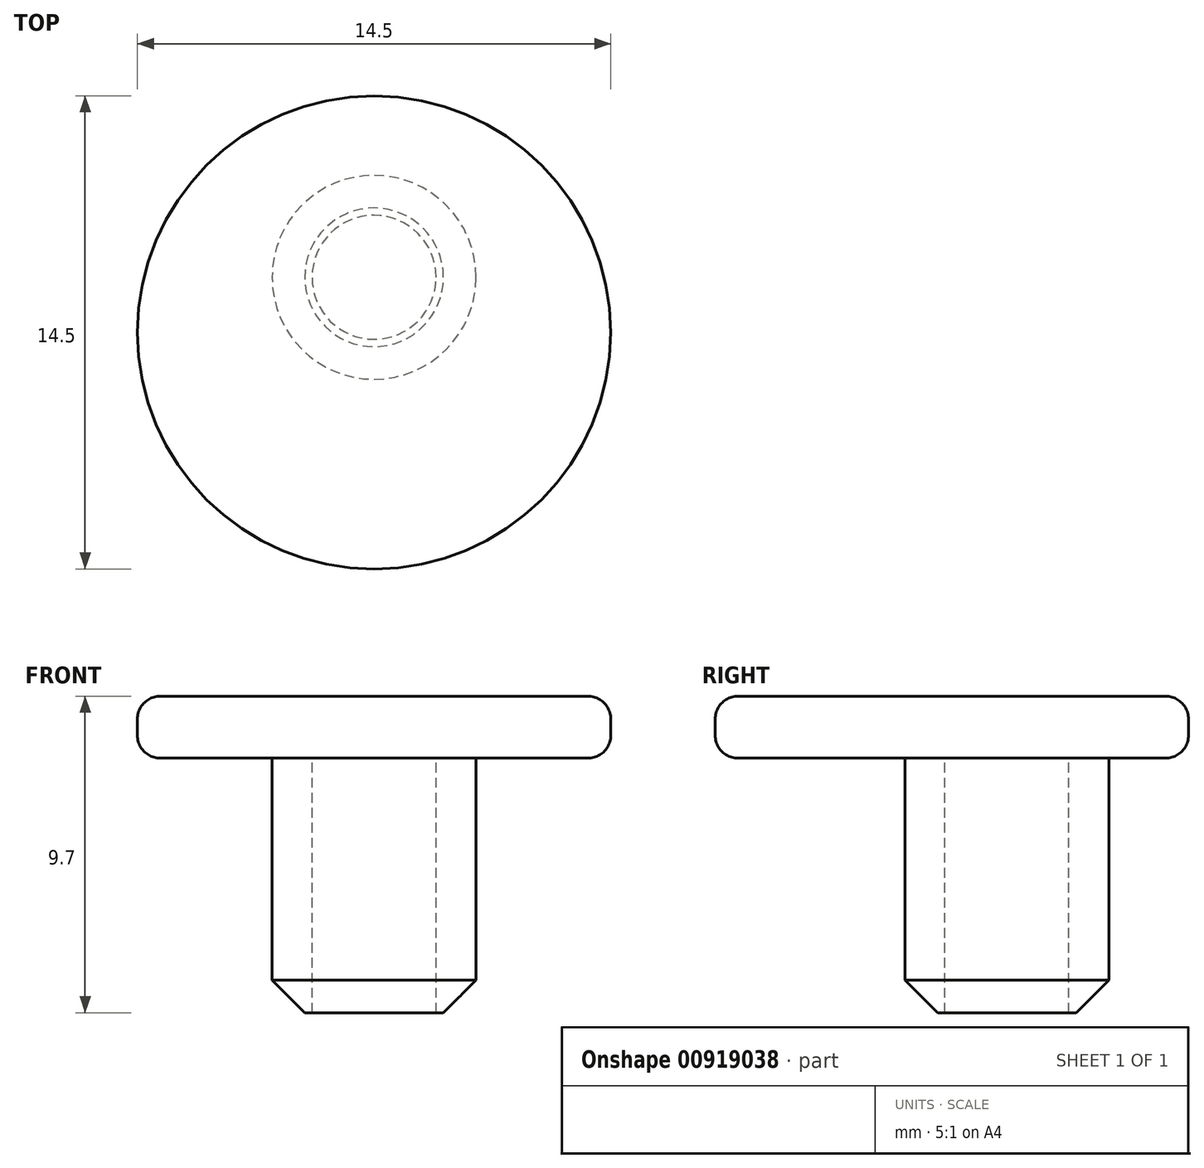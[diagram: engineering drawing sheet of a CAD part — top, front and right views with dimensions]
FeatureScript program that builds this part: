
annotation { "Feature Type Name" : "Feature", "Feature Type Description" : "" }
export const myFeature = defineFeature(function(context is Context, id is Id, definition is map)
    precondition{}
    {
        {
            var Q0;
            Q0=qCreatedBy(makeId("Top.planeOp"),FACE);
            var sketch = newSketch(context, id + "F0", { "sketchPlane" : qUnion([Q0])});
            skCircle(sketch, "E0", {"center": v(0, 0) * mm, "radius": 1.9 * mm});
            skCircle(sketch, "E1", {"center": v(0, 0) * mm, "radius": 3.12 * mm});
            skCircle(sketch, "E2", {"center": v(0, -1.7) * mm, "radius": 7.25 * mm});
            skLineSegment(sketch, "E3.bottom", {"start": v(-5.5, -3.2) * mm, "end": v(5.5, -3.2) * mm});
            skLineSegment(sketch, "E3.top", {"start": v(-5.5, -0.2) * mm, "end": v(5.5, -0.2) * mm});
            skLineSegment(sketch, "E3.left", {"start": v(-5.5, -3.2) * mm, "end": v(-5.5, -0.2) * mm});
            skLineSegment(sketch, "E3.right", {"start": v(5.5, -3.2) * mm, "end": v(5.5, -0.2) * mm});
            skLineSegment(sketch, "E4", {"start": v(0, -7.94) * mm, "end": v(-2.58, -5.2) * mm});
            skLineSegment(sketch, "E5", {"start": v(-2.58, -5.2) * mm, "end": v(2.58, -5.2) * mm});
            skLineSegment(sketch, "E6", {"start": v(2.58, -5.2) * mm, "end": v(0, -7.94) * mm});
            skSolve(sketch);
        }
        {
            var Q0;
            {var subQ0=sQuery(id+"F0.wireOp",EDGE,"E3.bottom");var subQ1=sQuery(id+"F0.wireOp",EDGE,"E0");var subQ2=makeQuery(id+"F0.imprint","INTERSECT",VERTEX,{"disambiguationData":[OD(0.0)],"derivedFrom":[subQ1,subQ0]});Q0=makeQuery(id+"F0.imprint","IMPRINT",FACE,{"disambiguationData":[TD([[makeQuery(id+"F0.imprint","IMPRINT",EDGE,{"disambiguationData":[TD([[subQ2,-1.0]])],"derivedFrom":subQ1}),-1.0]])]});}
            var Q1;
            {var subQ0=sQuery(id+"F0.wireOp",EDGE,"E3.top");var subQ1=sQuery(id+"F0.wireOp",EDGE,"E0");var subQ2=makeQuery(id+"F0.imprint","INTERSECT",VERTEX,{"disambiguationData":[OD(1.0)],"derivedFrom":[subQ1,subQ0]});Q1=makeQuery(id+"F0.imprint","IMPRINT",FACE,{"disambiguationData":[TD([[makeQuery(id+"F0.imprint","IMPRINT",EDGE,{"disambiguationData":[TD([[subQ2,1.0]])],"derivedFrom":subQ1}),-1.0]])]});}
            var Q2;
            {var subQ0=sQuery(id+"F0.wireOp",EDGE,"E3.top");var subQ1=sQuery(id+"F0.wireOp",EDGE,"E0");var subQ2=makeQuery(id+"F0.imprint","INTERSECT",VERTEX,{"disambiguationData":[OD(0.0)],"derivedFrom":[subQ1,subQ0]});Q2=makeQuery(id+"F0.imprint","IMPRINT",FACE,{"disambiguationData":[TD([[makeQuery(id+"F0.imprint","IMPRINT",EDGE,{"disambiguationData":[TD([[subQ2,1.0]])],"derivedFrom":subQ1}),-1.0]])]});}
            var Q3;
            {var subQ0=sQuery(id+"F0.wireOp",EDGE,"E3.top");var subQ1=sQuery(id+"F0.wireOp",EDGE,"E0");var subQ2=makeQuery(id+"F0.imprint","INTERSECT",VERTEX,{"disambiguationData":[OD(0.0)],"derivedFrom":[subQ1,subQ0]});Q3=makeQuery(id+"F0.imprint","IMPRINT",FACE,{"disambiguationData":[TD([[makeQuery(id+"F0.imprint","IMPRINT",EDGE,{"disambiguationData":[TD([[subQ2,-1.0]])],"derivedFrom":subQ1}),-1.0]])]});}
            extrude(context, id + "F1", {"entities" : qUnion([Q0, Q1, Q2, Q3]), "oppositeDirection" : true, "depth" : 7.8 * mm, "offsetDistance" : 25 * mm});
        }
        {
            var Q0;
            {var subQ0=sQuery(id+"F0.wireOp",EDGE,"E3.top");var subQ1=sQuery(id+"F0.wireOp",EDGE,"E0");var subQ2=makeQuery(id+"F0.imprint","INTERSECT",VERTEX,{"disambiguationData":[OD(0.0)],"derivedFrom":[subQ1,subQ0]});Q0=makeQuery(id+"F0.imprint","IMPRINT",FACE,{"disambiguationData":[TD([[makeQuery(id+"F0.imprint","IMPRINT",EDGE,{"disambiguationData":[TD([[subQ2,1.0]])],"derivedFrom":subQ1}),-1.0]])]});}
            var Q1;
            Q1=makeQuery(id+"F0.imprint","IMPRINT",FACE,{"disambiguationData":[TD([[makeQuery(id+"F0.imprint","IMPRINT",EDGE,{"derivedFrom":sQuery(id+"F0.wireOp",EDGE,"E2")}),1.0]])]});
            var Q2;
            {var subQ5=sQuery(id+"F0.wireOp",EDGE,"E3.left");Q2=makeQuery(id+"F0.imprint","IMPRINT",FACE,{"disambiguationData":[TD([[makeQuery(id+"F0.imprint","IMPRINT",EDGE,{"derivedFrom":subQ5}),-1.0]])]});}
            var Q3;
            {var subQ5=sQuery(id+"F0.wireOp",EDGE,"E3.right");Q3=makeQuery(id+"F0.imprint","IMPRINT",FACE,{"disambiguationData":[TD([[makeQuery(id+"F0.imprint","IMPRINT",EDGE,{"derivedFrom":subQ5}),1.0]])]});}
            var Q4;
            {var subQ0=sQuery(id+"F0.wireOp",EDGE,"E3.bottom");var subQ1=sQuery(id+"F0.wireOp",EDGE,"E0");var subQ2=makeQuery(id+"F0.imprint","INTERSECT",VERTEX,{"disambiguationData":[OD(0.0)],"derivedFrom":[subQ1,subQ0]});Q4=makeQuery(id+"F0.imprint","IMPRINT",FACE,{"disambiguationData":[TD([[makeQuery(id+"F0.imprint","IMPRINT",EDGE,{"disambiguationData":[TD([[subQ2,-1.0]])],"derivedFrom":subQ1}),-1.0]])]});}
            var Q5;
            {var subQ0=sQuery(id+"F0.wireOp",EDGE,"E3.top");var subQ1=sQuery(id+"F0.wireOp",EDGE,"E0");var subQ2=makeQuery(id+"F0.imprint","INTERSECT",VERTEX,{"disambiguationData":[OD(1.0)],"derivedFrom":[subQ1,subQ0]});Q5=makeQuery(id+"F0.imprint","IMPRINT",FACE,{"disambiguationData":[TD([[makeQuery(id+"F0.imprint","IMPRINT",EDGE,{"disambiguationData":[TD([[subQ2,1.0]])],"derivedFrom":subQ1}),-1.0]])]});}
            var Q6;
            {var subQ0=sQuery(id+"F0.wireOp",EDGE,"E3.top");var subQ1=sQuery(id+"F0.wireOp",EDGE,"E0");var subQ2=makeQuery(id+"F0.imprint","INTERSECT",VERTEX,{"disambiguationData":[OD(0.0)],"derivedFrom":[subQ1,subQ0]});Q6=makeQuery(id+"F0.imprint","IMPRINT",FACE,{"disambiguationData":[TD([[makeQuery(id+"F0.imprint","IMPRINT",EDGE,{"disambiguationData":[TD([[subQ2,-1.0]])],"derivedFrom":subQ1}),-1.0]])]});}
            var Q7;
            {var subQ0=sQuery(id+"F0.wireOp",EDGE,"E3.top");var subQ1=sQuery(id+"F0.wireOp",EDGE,"E0");var subQ2=makeQuery(id+"F0.imprint","INTERSECT",VERTEX,{"disambiguationData":[OD(0.0)],"derivedFrom":[subQ1,subQ0]});Q7=makeQuery(id+"F0.imprint","IMPRINT",FACE,{"disambiguationData":[TD([[makeQuery(id+"F0.imprint","IMPRINT",EDGE,{"disambiguationData":[TD([[subQ2,-1.0]])],"derivedFrom":subQ1}),1.0]])]});}
            var Q8;
            {var subQ0=sQuery(id+"F0.wireOp",EDGE,"E3.bottom");var subQ1=sQuery(id+"F0.wireOp",EDGE,"E0");var subQ2=makeQuery(id+"F0.imprint","INTERSECT",VERTEX,{"disambiguationData":[OD(0.0)],"derivedFrom":[subQ1,subQ0]});Q8=makeQuery(id+"F0.imprint","IMPRINT",FACE,{"disambiguationData":[TD([[makeQuery(id+"F0.imprint","IMPRINT",EDGE,{"disambiguationData":[TD([[subQ2,-1.0]])],"derivedFrom":subQ1}),1.0]])]});}
            var Q9;
            {var subQ0=sQuery(id+"F0.wireOp",EDGE,"E3.top");var subQ1=sQuery(id+"F0.wireOp",EDGE,"E0");var subQ2=makeQuery(id+"F0.imprint","INTERSECT",VERTEX,{"disambiguationData":[OD(0.0)],"derivedFrom":[subQ1,subQ0]});Q9=makeQuery(id+"F0.imprint","IMPRINT",FACE,{"disambiguationData":[TD([[makeQuery(id+"F0.imprint","IMPRINT",EDGE,{"disambiguationData":[TD([[subQ2,1.0]])],"derivedFrom":subQ1}),1.0]])]});}
            var Q10;
            Q10=makeQuery(id+"F0.imprint","IMPRINT",FACE,{"disambiguationData":[TD([[makeQuery(id+"F0.imprint","IMPRINT",EDGE,{"derivedFrom":sQuery(id+"F0.wireOp",EDGE,"E4")}),-1.0]])]});
            extrude(context, id + "F2", {"entities" : qUnion([Q0, Q1, Q2, Q3, Q4, Q5, Q6, Q7, Q8, Q9, Q10]), "depth" : 1.9 * mm, "offsetDistance" : 25 * mm});
        }
        {
            var Q0;
            Q0=makeQuery(id+"F1.opExtrude","CAP_EDGE",EDGE,{"disambiguationData":[OSD([sQuery(id+"F0.wireOp",EDGE,"E1")])],"isStart":false});
            chamfer(context, id + "F3", {"entities" : qUnion([Q0]), "width" : 1 * mm});
        }
        {
            var Q0;
            Q0=makeQuery(id+"F2.opExtrude","CAP_EDGE",EDGE,{"disambiguationData":[OSD([sQuery(id+"F0.wireOp",EDGE,"E2")])],"isStart":true});
            var Q1;
            Q1=makeQuery(id+"F2.opExtrude","CAP_EDGE",EDGE,{"disambiguationData":[OSD([sQuery(id+"F0.wireOp",EDGE,"E2")])],"isStart":false});
            fillet(context, id + "F4", {"entities" : qUnion([Q0, Q1]), "radius" : .7 * mm, "tangentPropagation" : true, "allowEdgeOverflow" : false});
        }
    });
